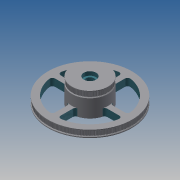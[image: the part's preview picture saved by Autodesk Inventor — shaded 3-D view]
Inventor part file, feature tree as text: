
AUTODESK INVENTOR PART (.ipt)
format: ipt  version: 2013 (Build 170138000, 138)  size: 1,584,640 bytes
history: native  units: mm
features: extrude x5, sketch x5, other x3, fillet x1, pattern_circular x1, projected_geometry x1
ambient origin geometry x8: Origin, YZ Plane, XZ Plane, XY Plane, X Axis, Y Axis, Z Axis, Center Point
bodies: Solid1 (feature_tree)
feature tree (16):
  other  "distal idler pulley.iam"
  other  "235 pulley blank.ipt:1"
  other  "100 pulley blank.ipt:1"
  extrude  "Extrusion1"  Depth=10.0mm TaperAngle=0.0deg
  extrude  "Extrusion2"  Depth=5.0mm
  fillet  "Fillet1"  [1 undecoded]
  pattern_circular  "Circular Pattern1"  Count=4 Angle=360.0deg
  extrude  "Extrusion3"  Depth=15.0mm
  extrude  "Extrusion4"  Depth=10.0mm TaperAngle=0.0deg
  extrude  "Extrusion5"  Depth=22.0mm
  sketch  "Sketch1"  dims[d0=10.0mm d1=10.0mm d2=0.0mm]
  projected_geometry  "Projected Loop1"
  sketch  "Sketch2"  dims[d3=5.0mm d4=5.0mm d5=0.0mm]
  sketch  "Sketch3"  dims[d6=12.0mm]
  sketch  "Sketch4"  dims[d7=10.0mm d8=0.0mm]
  sketch  "Sketch5"  dims[d9=5.0mm d10=40.0mm d11=360.0deg d13=15.0mm d15=10.0mm d16=0.0mm d17=22.0mm d19=7.0mm d20=0.0mm d21=22.0mm d23=7.0mm d24=0.0mm]
note: 1 required parameter value undecoded (feature->parameter linkage not recoverable at this tier; creation-order binding heuristic only, values carry confidence <= 0.55)
